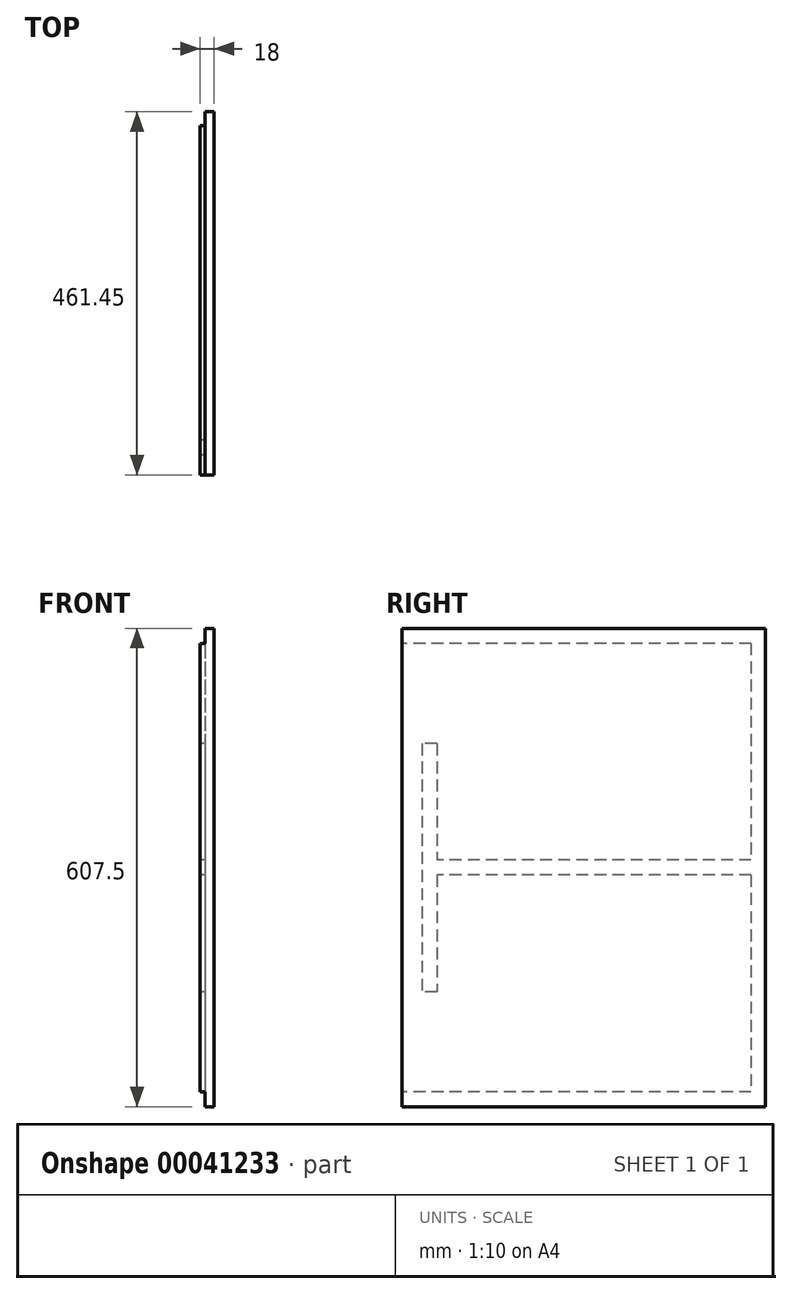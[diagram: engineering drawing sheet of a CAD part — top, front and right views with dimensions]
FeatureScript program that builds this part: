
annotation { "Feature Type Name" : "Feature", "Feature Type Description" : "" }
export const myFeature = defineFeature(function(context is Context, id is Id, definition is map)
    precondition{}
    {
        {
            var Q0;
            Q0=qCreatedBy(makeId("Right.planeOp"),FACE);
            var sketch = newSketch(context, id + "F0", { "sketchPlane" : qUnion([Q0])});
            skLineSegment(sketch, "E0.bottom", {"start": v(-223.91, 333.94) * mm, "end": v(237.54, 333.94) * mm});
            skLineSegment(sketch, "E0.top", {"start": v(-223.91, -273.56) * mm, "end": v(237.54, -273.56) * mm});
            skLineSegment(sketch, "E0.left", {"start": v(-223.91, 333.94) * mm, "end": v(-223.91, -273.56) * mm});
            skLineSegment(sketch, "E0.right", {"start": v(237.54, 333.94) * mm, "end": v(237.54, -273.56) * mm});
            skSolve(sketch);
        }
        {
            var Q0;
            Q0 = qSketchRegion(id + "F0", true);
            extrude(context, id + "F1", {"entities" : qUnion([Q0]), "depth" : 18 * mm});
        }
        {
            var Q0;
            Q0=makeQuery(id+"F1.opExtrude","CAP_FACE",FACE,{"disambiguationData":[OSD([sQuery(id+"F0.wireOp",EDGE,"E0.bottom"),sQuery(id+"F0.wireOp",EDGE,"E0.top"),sQuery(id+"F0.wireOp",EDGE,"E0.left"),sQuery(id+"F0.wireOp",EDGE,"E0.right")])],"isStart":true});
            var sketch = newSketch(context, id + "F2", { "sketchPlane" : qUnion([Q0])});
            skLineSegment(sketch, "E1.bottom", {"start": v(-237.54, 333.94) * mm, "end": v(223.91, 333.94) * mm});
            skLineSegment(sketch, "E1.top", {"start": v(-237.54, 314.94) * mm, "end": v(223.91, 314.94) * mm});
            skLineSegment(sketch, "E1.left", {"start": v(-237.54, 333.94) * mm, "end": v(-237.54, 314.94) * mm});
            skLineSegment(sketch, "E1.right", {"start": v(223.91, 333.94) * mm, "end": v(223.91, 314.94) * mm});
            skLineSegment(sketch, "E2.bottom", {"start": v(-237.54, -273.56) * mm, "end": v(223.91, -273.56) * mm});
            skLineSegment(sketch, "E2.top", {"start": v(-237.54, -254.56) * mm, "end": v(223.91, -254.56) * mm});
            skLineSegment(sketch, "E2.left", {"start": v(-237.54, -273.56) * mm, "end": v(-237.54, -254.56) * mm});
            skLineSegment(sketch, "E2.right", {"start": v(223.91, -273.56) * mm, "end": v(223.91, -254.56) * mm});
            skLineSegment(sketch, "E3.bottom", {"start": v(-237.54, 333.94) * mm, "end": v(-219.54, 333.94) * mm});
            skLineSegment(sketch, "E3.top", {"start": v(-237.54, -273.56) * mm, "end": v(-219.54, -273.56) * mm});
            skLineSegment(sketch, "E3.left", {"start": v(-237.54, 333.94) * mm, "end": v(-237.54, -273.56) * mm});
            skLineSegment(sketch, "E3.right", {"start": v(-219.54, 333.94) * mm, "end": v(-219.54, -273.56) * mm});
            skLineSegment(sketch, "E4.bottom", {"start": v(180.51, 333.94) * mm, "end": v(198.51, 333.94) * mm});
            skLineSegment(sketch, "E4.top", {"start": v(180.51, -273.56) * mm, "end": v(198.51, -273.56) * mm});
            skLineSegment(sketch, "E5.bottom", {"start": v(179.51, 187.9) * mm, "end": v(198.51, 187.9) * mm});
            skLineSegment(sketch, "E5.top", {"start": v(179.51, -127.5) * mm, "end": v(198.51, -127.5) * mm});
            skLineSegment(sketch, "E5.left", {"start": v(179.51, 187.9) * mm, "end": v(179.51, -127.5) * mm});
            skLineSegment(sketch, "E5.right", {"start": v(198.51, 187.9) * mm, "end": v(198.51, -127.5) * mm});
            skSolve(sketch);
        }
        {
            var Q0;
            Q0 = qSketchRegion(id + "F2", true);
            extrude(context, id + "F3", {"entities" : qUnion([Q0]), "operationType" : NewBodyOperationType.REMOVE, "oppositeDirection" : true, "depth" : 6 * mm});
        }
        {
            var Q0;
            Q0=makeQuery(id+"F1.opExtrude","CAP_FACE",FACE,{"disambiguationData":[OSD([sQuery(id+"F0.wireOp",EDGE,"E0.bottom"),sQuery(id+"F0.wireOp",EDGE,"E0.top"),sQuery(id+"F0.wireOp",EDGE,"E0.left"),sQuery(id+"F0.wireOp",EDGE,"E0.right")])],"isStart":true});
            var sketch = newSketch(context, id + "F4", { "sketchPlane" : qUnion([Q0])});
            skLineSegment(sketch, "E6", {"start": v(-219.54, 30.2) * mm, "end": v(179.51, 30.2) * mm, "construction": true});
            skLineSegment(sketch, "E7.bottom", {"start": v(-226.43, 39.7) * mm, "end": v(189.86, 39.7) * mm});
            skLineSegment(sketch, "E7.top", {"start": v(-226.43, 20.7) * mm, "end": v(189.86, 20.7) * mm});
            skLineSegment(sketch, "E7.left", {"start": v(-226.43, 39.7) * mm, "end": v(-226.43, 20.7) * mm});
            skLineSegment(sketch, "E7.right", {"start": v(189.86, 39.7) * mm, "end": v(189.86, 20.7) * mm});
            skSolve(sketch);
        }
        {
            var Q0;
            Q0 = qSketchRegion(id + "F4", true);
            extrude(context, id + "F5", {"entities" : qUnion([Q0]), "operationType" : NewBodyOperationType.REMOVE, "oppositeDirection" : true, "depth" : 6 * mm});
        }
    });
